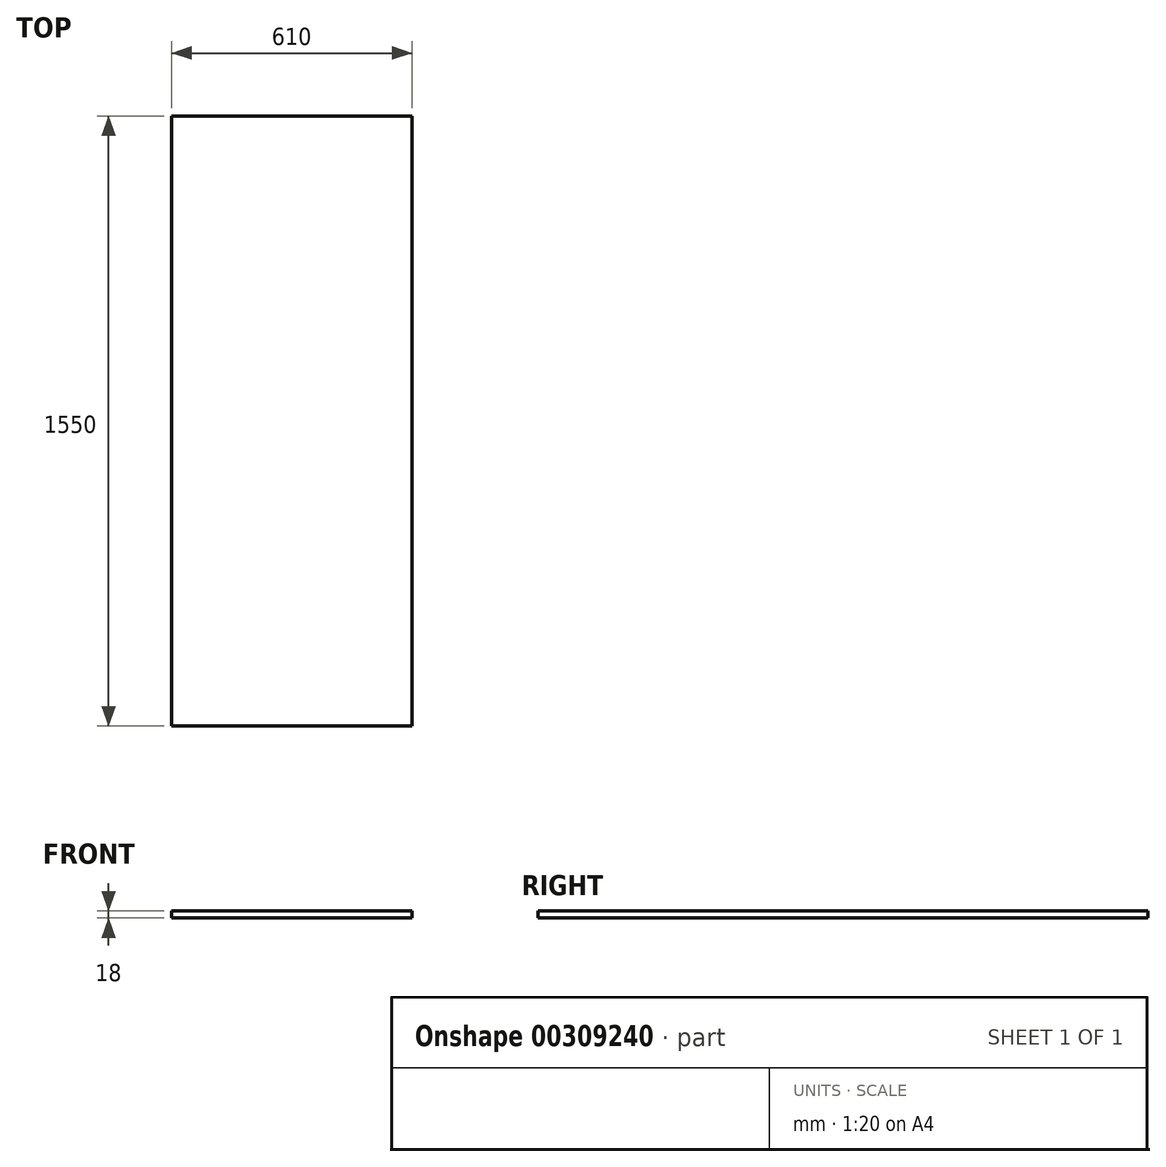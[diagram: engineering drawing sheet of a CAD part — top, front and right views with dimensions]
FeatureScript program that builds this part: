
annotation { "Feature Type Name" : "Feature", "Feature Type Description" : "" }
export const myFeature = defineFeature(function(context is Context, id is Id, definition is map)
    precondition{}
    {
        {
            var Q0;
            Q0=qCreatedBy(makeId("Right.planeOp"),FACE);
            var sketch = newSketch(context, id + "F0", { "sketchPlane" : qUnion([Q0])});
            skLineSegment(sketch, "E0.bottom", {"start": v(0, 0) * mm, "end": v(1550, 0) * mm});
            skLineSegment(sketch, "E0.top", {"start": v(0, 18) * mm, "end": v(1550, 18) * mm});
            skLineSegment(sketch, "E0.left", {"start": v(0, 0) * mm, "end": v(0, 18) * mm});
            skLineSegment(sketch, "E0.right", {"start": v(1550, 0) * mm, "end": v(1550, 18) * mm});
            skSolve(sketch);
        }
        {
            var Q0;
            Q0=makeQuery(id+"F0.imprint","IMPRINT",FACE,{"disambiguationData":[TD([[makeQuery(id+"F0.imprint","IMPRINT",EDGE,{"derivedFrom":sQuery(id+"F0.wireOp",EDGE,"E0.bottom")}),1.0]])]});
            extrude(context, id + "F1", {"entities" : qUnion([Q0]), "depth" : 610 * mm});
        }
    });
